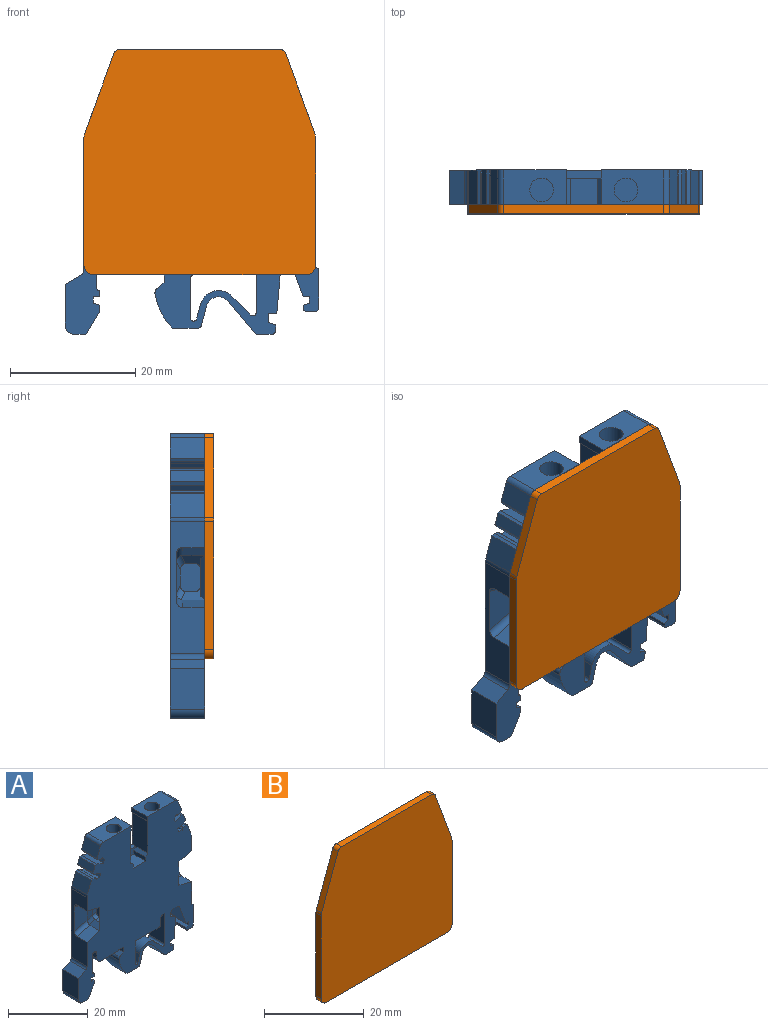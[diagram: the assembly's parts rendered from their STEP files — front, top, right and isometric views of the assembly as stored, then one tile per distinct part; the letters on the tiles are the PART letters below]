
ASSEMBLY  parts=2 mates=1
PART A: 172 faces, bbox 40.5x5.5x45.5 mm
  f0: plane 5.5x0.2mm, normal (0.71,0,-0.71), area 1.6mm2, adj f2,f76,f130,f163
  f1: plane 6x1.3mm, normal (0,0,1), area 7.8mm2, adj f2,f3,f118,f130
  f2: plane 9.8x5.5mm, normal (1,0,0), area 53.9mm2, adj f0,f1,f127,f130,f163
  f3: plane 9.8x5.5mm, normal (-1,0,0), area 53.9mm2, adj f1,f4,f110,f130,f163
  f4: plane 5.5x0.2mm, normal (-0.71,0,-0.71), area 1.6mm2, adj f3,f5,f130,f163
  f5: plane 5.5x1.3mm, normal (-1,0,0), area 7.1mm2, adj f4,f6,f130,f163
  f6: plane 10x5.5mm, normal (0,0,1), area 43.7mm2, adj f5,f7,f82,f130,f163
  f7: cylinder r=1mm len=5.5mm, axis (0,-1,0), area 6.7mm2, adj f6,f8,f130,f163
  f8: plane 5.5x3.29mm, normal (0.94,0,0.34), area 19.2mm2, adj f7,f115,f130,f163
  f9: plane 5.5x2.44mm, normal (0.34,0,-0.94), area 14.3mm2, adj f111,f112,f130,f163
  f10: cylinder r=0.6mm len=5.5mm, axis (0,-1,0), area 4.3mm2, adj f122,f123,f130,f163
  f11: plane 5.5x0.51mm, normal (-0.42,0,0.91), area 3.1mm2, adj f80,f130,f163,f165
  f12: plane 5.5x3.82mm, normal (0.94,0,0.34), area 22.4mm2, adj f13,f120,f130,f163
  f13: cylinder r=2mm len=5.5mm, axis (0,-1,0), area 3.8mm2, adj f12,f14,f130,f163
  f14: plane 20.61x5.5mm, normal (1,0,0), area 70.6mm2, adj f13,f15,f87,f93,f103,f105,f130,f150
  f15: plane 5.5x0.5mm, normal (0.5,0,0.87), area 3.2mm2, adj f14,f16,f130,f163
  f16: plane 6.31x5.5mm, normal (1,0,0), area 34.7mm2, adj f15,f17,f130,f163
  f17: cylinder r=0.5mm len=5.5mm, axis (0,-1,0), area 4.3mm2, adj f16,f18,f130,f163
  f18: plane 5.5x1.5mm, normal (0,0,-1), area 8.2mm2, adj f17,f19,f130,f163
  f19: cylinder r=0.5mm len=5.5mm, axis (0,-1,0), area 4.3mm2, adj f18,f20,f130,f163
  f20: plane 5.5x0.5mm, normal (-1,0,0), area 2.8mm2, adj f19,f21,f130,f163
  f21: plane 5.5x1mm, normal (-0.29,0,0.96), area 5.7mm2, adj f20,f22,f130,f163
  f22: plane 5.5x1mm, normal (-1,0,0), area 5.5mm2, adj f21,f23,f130,f163
  f23: plane 5.5x1mm, normal (0,0,-1), area 5.5mm2, adj f22,f24,f130,f163
  f24: plane 6.04x5.5mm, normal (-0.94,0,-0.34), area 35.4mm2, adj f23,f25,f130,f163
  f25: cylinder r=1mm len=5.5mm, axis (0,-1,0), area 6.7mm2, adj f24,f26,f130,f163
  f26: plane 5.5x1.11mm, normal (0,0,-1), area 6.1mm2, adj f25,f27,f130,f163
  f27: cylinder r=1.25mm len=5.5mm, axis (0,-1,0), area 22mm2, adj f26,f28,f130,f163
  f28: cylinder r=0.5mm len=5.5mm, axis (0,-1,0), area 4.7mm2, adj f27,f29,f130,f163
  f29: plane 6.26x5.5mm, normal (1,0,-0.09), area 34.6mm2, adj f28,f30,f130,f163
  f30: plane 5.5x1.3mm, normal (0,0,-1), area 7.1mm2, adj f29,f31,f130,f163
  f31: plane 5.5x1.5mm, normal (1,0,0), area 8.2mm2, adj f30,f32,f130,f163
  f32: plane 5.5x1.14mm, normal (0.29,0,0.96), area 6.5mm2, adj f31,f33,f130,f163
  f33: plane 5.5x1.1mm, normal (1,0,-0.09), area 6.1mm2, adj f32,f34,f130,f163
  f34: cylinder r=0.5mm len=5.5mm, axis (0,-1,0), area 4.1mm2, adj f33,f35,f130,f163
  f35: plane 5.5x2.31mm, normal (0,0,-1), area 12.7mm2, adj f34,f36,f130,f163
  f36: cylinder r=0.5mm len=5.5mm, axis (0,-1,0), area 2.4mm2, adj f35,f37,f130,f163
  f37: plane 5.5x5.11mm, normal (-0.76,0,-0.65), area 36.8mm2, adj f36,f38,f130,f163
  f38: cylinder r=2mm len=5.5mm, axis (0,-1,0), area 24mm2, adj f37,f39,f130,f163
  f39: plane 5.5x3.15mm, normal (0.97,0,-0.26), area 17.9mm2, adj f38,f40,f130,f163
  f40: cylinder r=0.5mm len=5.5mm, axis (0,-1,0), area 3.6mm2, adj f39,f41,f130,f163
  f41: plane 5.5x4.08mm, normal (0,0,-1), area 22.5mm2, adj f40,f42,f130,f163
  f42: cylinder r=10mm len=5.5mm, axis (0,-1,0), area 34.2mm2, adj f41,f43,f130,f163
  f43: cylinder r=1mm len=5.5mm, axis (0,-1,0), area 5.7mm2, adj f42,f44,f130,f163
  f44: plane 5.5x1.12mm, normal (-0.64,0,0.77), area 8mm2, adj f43,f45,f130,f163
  f45: plane 5.5x1.2mm, normal (-1,0,0), area 6.6mm2, adj f44,f46,f130,f163
  f46: cylinder r=0.3mm len=5.5mm, axis (0,-1,0), area 2.6mm2, adj f45,f47,f130,f163
  f47: plane 5.5x1.2mm, normal (0,0,-1), area 6.6mm2, adj f46,f48,f130,f163
  f48: plane 5.5x0.3mm, normal (1,0,0), area 1.7mm2, adj f47,f49,f130,f163
  f49: plane 6.3x5.5mm, normal (0,0,-1), area 34.6mm2, adj f48,f50,f130,f163
  f50: cylinder r=1.5mm len=5.5mm, axis (0,-1,0), area 13mm2, adj f49,f51,f130,f163
  f51: plane 5.5x1.75mm, normal (-1,0,0), area 9.6mm2, adj f50,f52,f130,f163
  f52: cylinder r=0.75mm len=5.5mm, axis (0,-1,0), area 13mm2, adj f51,f53,f130,f163
  f53: plane 5.5x5.25mm, normal (1,0,0), area 28.9mm2, adj f52,f54,f130,f163
  f54: cylinder r=0.5mm len=5.5mm, axis (0,-1,0), area 4.3mm2, adj f53,f55,f130,f163
  f55: plane 5.5x1mm, normal (1,0,0), area 5.5mm2, adj f54,f56,f130,f163
  f56: plane 5.5x1mm, normal (0,0,-1), area 5.5mm2, adj f55,f57,f130,f163
  f57: plane 5.5x1mm, normal (1,0,0), area 5.5mm2, adj f56,f58,f130,f163
  f58: plane 5.5x1mm, normal (0.29,0,0.96), area 5.8mm2, adj f57,f59,f130,f163
  f59: plane 5.5x0.99mm, normal (1,0,0), area 5.5mm2, adj f58,f60,f130,f163
  f60: plane 5.5x3.45mm, normal (0.87,0,-0.5), area 21.9mm2, adj f59,f61,f130,f163
  f61: cylinder r=0.5mm len=5.5mm, axis (0,-1,0), area 2.9mm2, adj f60,f62,f130,f163
  f62: plane 5.5x1.58mm, normal (0,0,-1), area 8.7mm2, adj f61,f63,f130,f163
  f63: cylinder r=1.5mm len=5.5mm, axis (0,-1,0), area 13mm2, adj f62,f64,f130,f163
  f64: plane 6.5x5.5mm, normal (-1,0,0), area 35.8mm2, adj f63,f66,f130,f163
  f65: cylinder r=1mm len=5.5mm, axis (0,-1,0), area 5.8mm2, adj f66,f128,f130,f163
  f66: plane 5.5x2.5mm, normal (-0.5,0,0.87), area 15.9mm2, adj f64,f65,f130,f163
  f67: plane 4.5x3.3mm, normal (1,0,0), area 14mm2, adj f78,f84,f92,f94,f96,f104,f106,f131
  f68: cylinder r=2mm len=5.5mm, axis (0,-1,0), area 3.8mm2, adj f128,f130,f163,f165
  f69: plane 5.5x1.14mm, normal (0.17,0,0.98), area 6.4mm2, adj f111,f121,f130,f163
  f70: plane 5.5x0.51mm, normal (-0.91,0,-0.42), area 3.1mm2, adj f130,f142,f163,f164
  f71: plane 4.2x1.2mm, normal (1,0,0), area 5mm2, adj f118,f125,f127,f163
  f72: plane 5.5x1.88mm, normal (-0.94,0,0.34), area 11mm2, adj f113,f124,f130,f163
  f73: cylinder r=0.6mm len=5.5mm, axis (0,-1,0), area 4.3mm2, adj f80,f114,f130,f163
  f74: cylinder r=1mm len=5.5mm, axis (0,-1,0), area 6.7mm2, adj f75,f130,f163,f164
  f75: plane 10x5.5mm, normal (0,0,1), area 43.7mm2, adj f74,f76,f85,f130,f163
  f76: plane 5.5x1.3mm, normal (1,0,0), area 7.1mm2, adj f0,f75,f130,f163
  f77: plane 3.8x3.8mm, normal (0,0,1), area 11.3mm2, adj f85
  f78: cylinder r=1mm len=1.5mm, axis (-1,0,0), area 2.3mm2, adj f67,f83,f92,f106,f154
  f79: cylinder r=0.6mm len=5.5mm, axis (0,-1,0), area 4.3mm2, adj f95,f130,f142,f163
  f80: plane 5.5x0.96mm, normal (0.34,0,0.94), area 5.6mm2, adj f11,f73,f130,f163
  f81: plane 5.5x1.88mm, normal (0.94,0,0.34), area 11mm2, adj f88,f112,f130,f163
  f82: cylinder r=1.9mm len=5.5mm, axis (0,0,1), area 65.7mm2, adj f6,f108
  f83: plane 3.74x2.36mm, normal (0.72,0,0.7), area 5.8mm2, adj f78,f87,f92,f93,f94,f96,f102,f154
  f84: cylinder r=1mm len=1.5mm, axis (-1,0,0), area 2.3mm2, adj f67,f90,f104,f106,f147
  f85: cylinder r=1.9mm len=5.5mm, axis (0,0,1), area 65.7mm2, adj f75,f77
  f86: plane 1.5x1.3mm, normal (0,0,-1), area 1.9mm2, adj f97,f99,f100,f160
  f87: cylinder r=1mm len=5.02mm, axis (0.97,0,-0.26), area 7.4mm2, adj f14,f83,f93,f103,f135,f154
  f88: plane 5.5x0.51mm, normal (0.42,0,0.91), area 3.1mm2, adj f81,f117,f130,f163
  f89: plane 5.5x1.01mm, normal (-0.94,0,0.34), area 5.9mm2, adj f91,f114,f130,f163
  f90: plane 3.74x2.36mm, normal (0.72,0,-0.7), area 5.8mm2, adj f84,f96,f102,f104,f105,f131,f147,f150
  f91: plane 5.5x2.44mm, normal (-0.34,0,-0.94), area 14.3mm2, adj f89,f124,f130,f163
  f92: plane 1.5x1.3mm, normal (0,0,1), area 1.9mm2, adj f67,f78,f83,f94
  f93: plane 4.5x3.5mm, normal (0.26,0,0.97), area 16.3mm2, adj f14,f83,f87,f163
  f94: cylinder r=1mm len=1.5mm, axis (1,0,0), area 1.8mm2, adj f67,f83,f92,f96
  f95: plane 5.5x0.88mm, normal (-0.77,0,-0.64), area 6.4mm2, adj f79,f119,f130,f163
  f96: plane 5.95x2.2mm, normal (0,1,0), area 8.4mm2, adj f67,f83,f90,f94,f102,f131
  f97: plane 4.5x3.3mm, normal (-1,0,0), area 14mm2, adj f86,f98,f100,f101,f136,f137,f156,f160
  f98: plane 5.95x2.2mm, normal (0,1,0), area 8.4mm2, adj f97,f99,f100,f101,f155,f161
  f99: plane 3.74x2.36mm, normal (-0.72,0,-0.7), area 5.8mm2, adj f86,f98,f100,f134,f138,f144,f160,f161
  f100: cylinder r=1mm len=1.5mm, axis (1,0,0), area 1.8mm2, adj f86,f97,f98,f99
  f101: cylinder r=1mm len=1.5mm, axis (-1,0,0), area 1.8mm2, adj f97,f98,f155,f156
  f102: plane 7.19x0.6mm, normal (0.71,0.71,0), area 5.6mm2, adj f83,f90,f96,f163
  f103: plane 7.53x4.5mm, normal (0,-1,0), area 28.5mm2, adj f14,f87,f105,f135
  f104: plane 1.5x1.3mm, normal (0,0,-1), area 1.9mm2, adj f67,f84,f90,f131
  f105: cylinder r=1mm len=5.02mm, axis (0.97,0,0.26), area 7.4mm2, adj f14,f90,f103,f135,f147,f150
  f106: plane 2.5x1.5mm, normal (0,-1,0), area 3.8mm2, adj f67,f78,f84,f135,f147,f154
  f107: plane 5.5x2.44mm, normal (0.34,0,0.94), area 14.3mm2, adj f113,f119,f130,f163
  f108: plane 3.8x3.8mm, normal (0,0,1), area 11.3mm2, adj f82
  f109: plane 5.5x0.96mm, normal (-0.34,0,0.94), area 5.6mm2, adj f120,f121,f130,f163
  f110: plane 4.2x0.8mm, normal (-0.71,0,0.71), area 4.8mm2, adj f3,f118,f126,f163
  f111: plane 5.5x1.01mm, normal (0.94,0,0.34), area 5.9mm2, adj f9,f69,f130,f163
  f112: plane 5.5x0.51mm, normal (0.91,0,-0.42), area 3.1mm2, adj f9,f81,f130,f163
  f113: plane 5.5x0.51mm, normal (-0.42,0,0.91), area 3.1mm2, adj f72,f107,f130,f163
  f114: plane 5.5x1.14mm, normal (-0.17,0,0.98), area 6.4mm2, adj f73,f89,f130,f163
  f115: plane 5.5x0.51mm, normal (0.91,0,-0.42), area 3.1mm2, adj f8,f122,f130,f163
  f116: plane 5.5x1.01mm, normal (0.94,0,0.34), area 5.9mm2, adj f117,f123,f130,f163
  f117: plane 5.5x2.44mm, normal (-0.34,0,0.94), area 14.3mm2, adj f88,f116,f130,f163
  f118: plane 6x2mm, normal (0,-1,0), area 9.4mm2, adj f1,f71,f110,f125,f126,f127
  f119: plane 5.5x1.01mm, normal (-0.94,0,0.34), area 5.9mm2, adj f95,f107,f130,f163
  f120: plane 5.5x0.51mm, normal (0.42,0,0.91), area 3.1mm2, adj f12,f109,f130,f163
  f121: cylinder r=0.6mm len=5.5mm, axis (0,-1,0), area 4.3mm2, adj f69,f109,f130,f163
  f122: plane 5.5x0.96mm, normal (0.34,0,-0.94), area 5.6mm2, adj f10,f115,f130,f163
  f123: plane 5.5x0.88mm, normal (0.77,0,-0.64), area 6.4mm2, adj f10,f116,f130,f163
  f124: plane 5.5x0.51mm, normal (-0.91,0,-0.42), area 3.1mm2, adj f72,f91,f130,f163
  f125: plane 4.4x4.2mm, normal (0,0,1), area 18.5mm2, adj f71,f118,f126,f163
  f126: plane 4.2x1.2mm, normal (-1,0,0), area 5mm2, adj f110,f118,f125,f163
  f127: plane 4.2x0.8mm, normal (0.71,0,0.71), area 4.8mm2, adj f2,f71,f118,f163
  f128: plane 21.1x5.5mm, normal (-1,0,0), area 73.3mm2, adj f65,f68,f130,f138,f144,f145,f158,f159
  f129: plane 5.18x1.3mm, normal (-0.42,-0.91,0), area 5.5mm2, adj f134,f136,f138,f145,f157,f159
  f130: plane 45.5x40.5mm, normal (0,1,0), area 1306.7mm2, adj f0,f1,f2,f3,f4,f5,f6,f7
  f131: cylinder r=1mm len=1.5mm, axis (-1,0,0), area 1.8mm2, adj f67,f90,f96,f104
  f132: plane 5.5x1.9mm, normal (1,0,0), area 10.4mm2, adj f130,f133,f139,f163
  f133: cylinder r=0.5mm len=5.5mm, axis (0,-1,0), area 4.3mm2, adj f130,f132,f151,f163
  f134: cylinder r=1mm len=2.32mm, axis (0.66,-0.31,-0.68), area 2.5mm2, adj f99,f129,f136,f138,f160
  f135: plane 5.18x1.3mm, normal (0.42,-0.91,0), area 5.5mm2, adj f87,f103,f105,f106,f147,f154
  f136: plane 2.5x1.5mm, normal (0,-1,0), area 3.8mm2, adj f97,f129,f134,f137,f157,f160
  f137: cylinder r=1mm len=1.5mm, axis (1,0,0), area 2.3mm2, adj f97,f136,f155,f156,f157
  f138: cylinder r=1mm len=5.02mm, axis (-0.97,0,0.26), area 7.4mm2, adj f99,f128,f129,f134,f144,f159
  f139: cylinder r=0.8mm len=5.5mm, axis (0,-1,0), area 6.9mm2, adj f130,f132,f148,f163
  f140: plane 5.5x2.31mm, normal (-0.97,0,0.26), area 13.2mm2, adj f130,f141,f146,f163
  f141: cylinder r=0.5mm len=5.5mm, axis (0,-1,0), area 7.9mm2, adj f130,f140,f162,f163
  f142: plane 5.5x0.96mm, normal (-0.34,0,-0.94), area 5.6mm2, adj f70,f79,f130,f163
  f143: cylinder r=0.5mm len=5.5mm, axis (0,-1,0), area 6.5mm2, adj f130,f152,f153,f163
  f144: plane 4.5x3.5mm, normal (-0.26,0,-0.97), area 16.3mm2, adj f99,f128,f138,f163
  f145: cylinder r=1mm len=5.02mm, axis (-0.97,0,-0.26), area 7.4mm2, adj f128,f129,f155,f157,f158,f159
  f146: cylinder r=3mm len=5.5mm, axis (0,-1,0), area 34.6mm2, adj f130,f140,f153,f163
  f147: cylinder r=1mm len=2.32mm, axis (0.66,0.31,0.68), area 2.5mm2, adj f84,f90,f105,f106,f135
  f148: plane 5.5x0.7mm, normal (0,0,-1), area 3.8mm2, adj f130,f139,f152,f163
  f149: cylinder r=0.5mm len=5.5mm, axis (0,-1,0), area 4.3mm2, adj f130,f151,f162,f163
  f150: plane 4.5x3.5mm, normal (0.26,0,-0.97), area 16.3mm2, adj f14,f90,f105,f163
  f151: plane 8x5.5mm, normal (0,0,-1), area 44mm2, adj f130,f133,f149,f163
  f152: plane 9.25x5.5mm, normal (-1,0,0), area 50.9mm2, adj f130,f143,f148,f163
  f153: plane 5.5x3.03mm, normal (0.71,0,0.71), area 23.5mm2, adj f130,f143,f146,f163
  f154: cylinder r=1mm len=2.32mm, axis (-0.66,-0.31,0.68), area 2.5mm2, adj f78,f83,f87,f106,f135
  f155: plane 3.74x2.36mm, normal (-0.72,0,0.7), area 5.8mm2, adj f98,f101,f137,f145,f156,f157,f158,f161
  f156: plane 1.5x1.3mm, normal (0,0,1), area 1.9mm2, adj f97,f101,f137,f155
  f157: cylinder r=1mm len=2.32mm, axis (0.66,-0.31,0.68), area 2.5mm2, adj f129,f136,f137,f145,f155
  f158: plane 4.5x3.5mm, normal (-0.26,0,0.97), area 16.3mm2, adj f128,f145,f155,f163
  f159: plane 7.53x4.5mm, normal (0,-1,0), area 28.5mm2, adj f128,f129,f138,f145
  f160: cylinder r=1mm len=1.5mm, axis (1,0,0), area 2.3mm2, adj f86,f97,f99,f134,f136
  f161: plane 7.19x0.6mm, normal (-0.71,0.71,0), area 5.6mm2, adj f98,f99,f155,f163
  f162: plane 6.41x5.5mm, normal (1,0,0), area 35.2mm2, adj f130,f141,f149,f163
  f163: plane 45.5x40.5mm, normal (0,-1,0), area 1221.7mm2, adj f0,f2,f3,f4,f5,f6,f7,f8
  f164: plane 5.5x3.29mm, normal (-0.94,0,0.34), area 19.2mm2, adj f70,f74,f130,f163
  f165: plane 5.5x3.82mm, normal (-0.94,0,0.34), area 22.4mm2, adj f11,f68,f130,f163
  f166: cylinder r=1.5mm len=3mm, axis (0,-1,0), area 7.5mm2, adj f167,f168
  f167: plane 3x3mm, normal (0,1,0), area 7.1mm2, adj f166
  f168: plane 3x3mm, normal (0,-1,0), area 7.1mm2, adj f166
  f169: cylinder r=1.5mm len=3mm, axis (0,-1,0), area 7.5mm2, adj f170,f171
  f170: plane 3x3mm, normal (0,1,0), area 7.1mm2, adj f169
  f171: plane 3x3mm, normal (0,-1,0), area 7.1mm2, adj f169
PART B: 14 faces, bbox 37x1.5x36 mm
  f0: plane 34x1.5mm, normal (0,0,-1), area 51mm2, adj f4,f5,f12,f13
  f1: plane 20.41x1.5mm, normal (1,0,0), area 30.6mm2, adj f4,f11,f12,f13
  f2: plane 20.41x1.5mm, normal (-1,0,0), area 30.6mm2, adj f5,f10,f12,f13
  f3: plane 25.6x1.5mm, normal (0,0,1), area 38.4mm2, adj f8,f9,f12,f13
  f4: cylinder r=1.5mm len=1.5mm, axis (0,-1,0), area 3.5mm2, adj f0,f1,f12,f13
  f5: cylinder r=1.5mm len=1.5mm, axis (0,-1,0), area 3.5mm2, adj f0,f2,f12,f13
  f6: plane 12.75x4.64mm, normal (0.94,0,0.34), area 20.3mm2, adj f9,f11,f12,f13
  f7: plane 12.75x4.64mm, normal (-0.94,0,0.34), area 20.3mm2, adj f8,f10,f12,f13
  f8: cylinder r=1mm len=1.5mm, axis (0,1,0), area 1.8mm2, adj f3,f7,f12,f13
  f9: cylinder r=1mm len=1.5mm, axis (0,-1,0), area 1.8mm2, adj f3,f6,f12,f13
  f10: cylinder r=2mm len=1.5mm, axis (0,1,0), area 1mm2, adj f2,f7,f12,f13
  f11: cylinder r=2mm len=1.5mm, axis (0,1,0), area 1mm2, adj f1,f6,f12,f13
  f12: plane 37x36mm, normal (0,-1,0), area 1262.2mm2, adj f0,f1,f2,f3,f4,f5,f6,f7
  f13: plane 37x36mm, normal (0,1,0), area 1262.2mm2, adj f0,f1,f2,f3,f4,f5,f6,f7
PLACE A t=(-6.87,1.01,-0.57)mm
PLACE B t=(-6.87,1.01,-0.57)mm
MATE fastened B.f13 <-> A.f163  axis (0,1,0) through (6.87,1.01,34.77)mm
